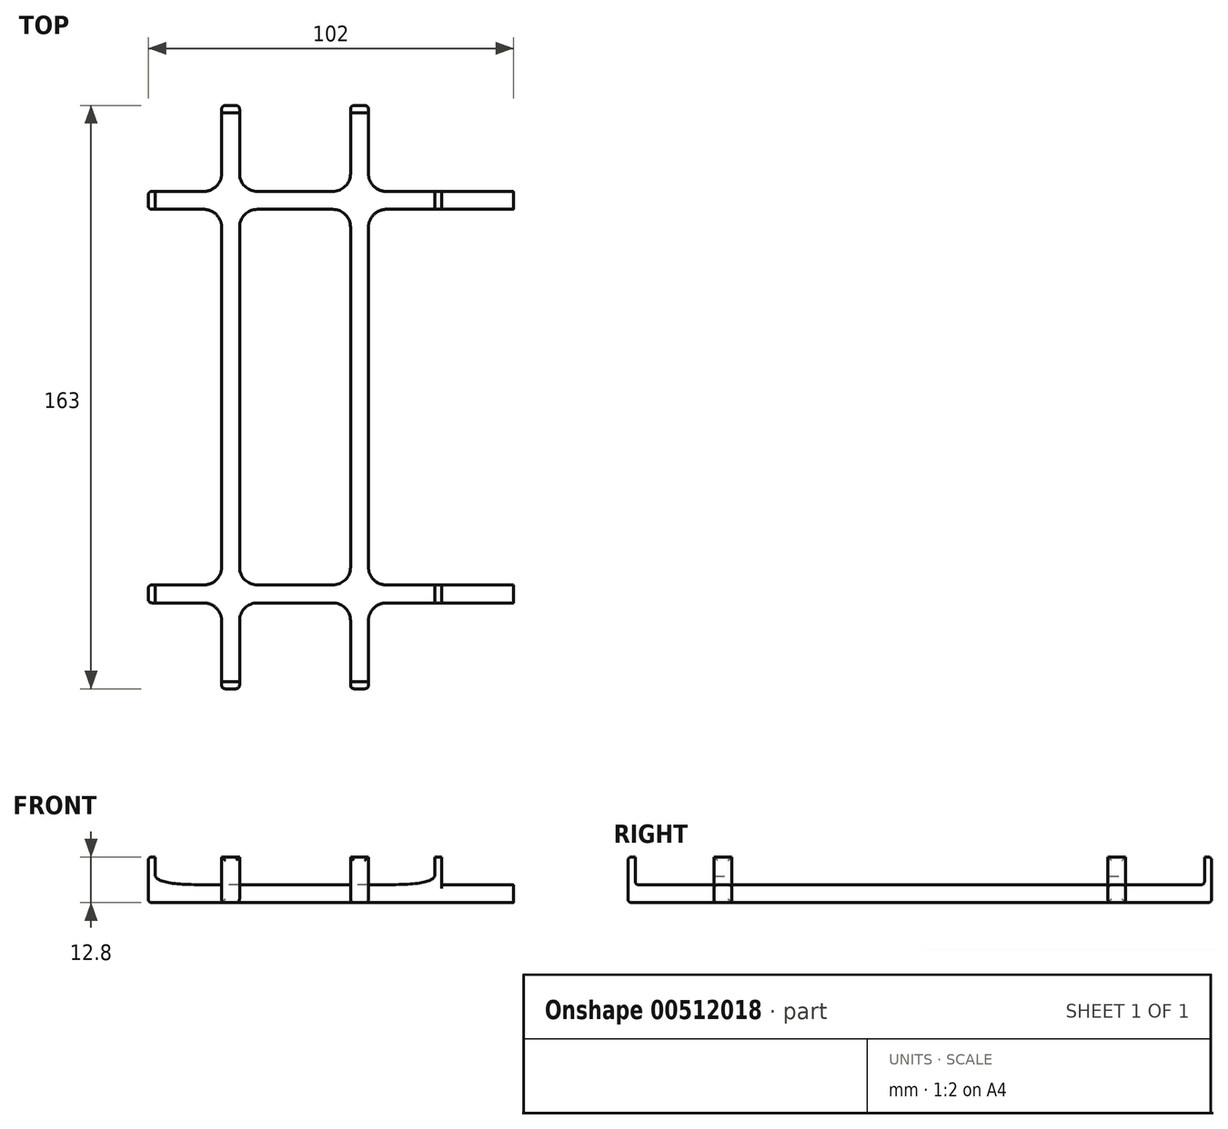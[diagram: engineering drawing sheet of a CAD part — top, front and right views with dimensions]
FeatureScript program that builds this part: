
annotation { "Feature Type Name" : "Feature", "Feature Type Description" : "" }
export const myFeature = defineFeature(function(context is Context, id is Id, definition is map)
    precondition{}
    {
        {
            var Q0;
            Q0=qCreatedBy(makeId("Front.planeOp"),FACE);
            var sketch = newSketch(context, id + "F0", { "sketchPlane" : qUnion([Q0])});
            skLineSegment(sketch, "E0", {"start": v(-41, 7.8) * mm, "end": v(-41, -5) * mm});
            skLineSegment(sketch, "E1", {"start": v(-41, -5) * mm, "end": v(41, -5) * mm});
            skLineSegment(sketch, "E2", {"start": v(41, -5) * mm, "end": v(41, 7.8) * mm});
            skLineSegment(sketch, "E3", {"start": v(41, 7.8) * mm, "end": v(39, 7.8) * mm});
            skLineSegment(sketch, "E4", {"start": v(39, 7.8) * mm, "end": v(39, 0) * mm});
            skLineSegment(sketch, "E5", {"start": v(39, 0) * mm, "end": v(-39, 0) * mm});
            skLineSegment(sketch, "E6", {"start": v(-39, 0) * mm, "end": v(-39, 7.8) * mm});
            skLineSegment(sketch, "E7", {"start": v(-39, 7.8) * mm, "end": v(-41, 7.8) * mm});
            skPoint(sketch, "E8", {"position": v(0, 0) * mm});
            skFitSpline(sketch, "E9", {"points": [v(-39, 2.4) * mm, v(-21, 0) * mm], "startDerivative": vector(3.6, -7.2) * mm, "endDerivative": vector(27, 0) * mm});
            skFitSpline(sketch, "E10.MirrorCS", {"points": [v(39, 2.4) * mm, v(21, 0) * mm], "startDerivative": vector(-3.6, -7.2) * mm, "endDerivative": vector(-27, 0) * mm});
            skSolve(sketch);
        }
        {
            var Q0;
            Q0=makeQuery(id+"F0.imprint","IMPRINT",FACE,{"disambiguationData":[TD([[makeQuery(id+"F0.imprint","IMPRINT",EDGE,{"derivedFrom":sQuery(id+"F0.wireOp",EDGE,"E0")}),1.0]])]});
            var Q1;
            {var subQ3=sQuery(id+"F0.wireOp",EDGE,"E9");Q1=makeQuery(id+"F0.imprint","IMPRINT",FACE,{"disambiguationData":[TD([[makeQuery(id+"F0.imprint","IMPRINT",EDGE,{"derivedFrom":subQ3}),-1.0]])]});}
            var Q2;
            {var subQ3=sQuery(id+"F0.wireOp",EDGE,"E10.MirrorCS");Q2=makeQuery(id+"F0.imprint","IMPRINT",FACE,{"disambiguationData":[TD([[makeQuery(id+"F0.imprint","IMPRINT",EDGE,{"derivedFrom":subQ3}),1.0]])]});}
            extrude(context, id + "F1", {"entities" : qUnion([Q0, Q1, Q2]), "depth" : 5 * mm, "symmetric" : true});
        }
        {
            var Q0;
            Q0=qCreatedBy(makeId("Right.planeOp"),FACE);
            var sketch = newSketch(context, id + "F2", { "sketchPlane" : qUnion([Q0])});
            skLineSegment(sketch, "E11", {"start": v(-81.5, 7.8) * mm, "end": v(-81.5, -5) * mm});
            skLineSegment(sketch, "E12", {"start": v(-81.5, -5) * mm, "end": v(81.5, -5) * mm});
            skLineSegment(sketch, "E13", {"start": v(81.5, -5) * mm, "end": v(81.5, 7.8) * mm});
            skLineSegment(sketch, "E14", {"start": v(81.5, 7.8) * mm, "end": v(79.5, 7.8) * mm});
            skLineSegment(sketch, "E15", {"start": v(79.5, 7.8) * mm, "end": v(79.5, 0) * mm});
            skLineSegment(sketch, "E16", {"start": v(79.5, 0) * mm, "end": v(-79.5, 0) * mm});
            skLineSegment(sketch, "E17", {"start": v(-79.5, 0) * mm, "end": v(-79.5, 7.8) * mm});
            skLineSegment(sketch, "E18", {"start": v(-79.5, 7.8) * mm, "end": v(-81.5, 7.8) * mm});
            skPoint(sketch, "E19", {"position": v(0, 0) * mm});
            skSolve(sketch);
        }
        {
            var Q0;
            Q0=makeQuery(id+"F2.imprint","IMPRINT",FACE,{"disambiguationData":[TD([[makeQuery(id+"F2.imprint","IMPRINT",EDGE,{"derivedFrom":sQuery(id+"F2.wireOp",EDGE,"E11")}),1.0]])]});
            extrude(context, id + "F3", {"entities" : qUnion([Q0]), "depth" : 5 * mm, "symmetric" : true});
        }
        {
            var Q0;
            Q0=makeQuery(id+"F1.opExtrude","SWEPT_BODY",BODY,{"disambiguationData":[OSD([sQuery(id+"F0.wireOp",EDGE,"E0"),sQuery(id+"F0.wireOp",EDGE,"E1"),sQuery(id+"F0.wireOp",EDGE,"E2"),sQuery(id+"F0.wireOp",EDGE,"E3"),sQuery(id+"F0.wireOp",EDGE,"E4"),sQuery(id+"F0.wireOp",EDGE,"E5"),sQuery(id+"F0.wireOp",EDGE,"E6"),sQuery(id+"F0.wireOp",EDGE,"E7"),sQuery(id+"F0.wireOp",EDGE,"E9"),sQuery(id+"F0.wireOp",EDGE,"E10.MirrorCS")])]});
            var Q1;
            Q1=makeQuery(id+"F3.opExtrude","CAP_EDGE",EDGE,{"disambiguationData":[OSD([sQuery(id+"F2.wireOp",EDGE,"E16")])],"isStart":false});
            transform(context, id + "F4", {"entities" : qUnion([Q0]), "transformType" : TransformType.TRANSLATION_DISTANCE, "transformDirection" : qUnion([Q1]), "distance" : 55 * mm, "makeCopy" : false});
        }
        {
            var Q0;
            Q0=makeQuery(id+"F1.opExtrude","SWEPT_BODY",BODY,{"disambiguationData":[OSD([sQuery(id+"F0.wireOp",EDGE,"E0"),sQuery(id+"F0.wireOp",EDGE,"E1"),sQuery(id+"F0.wireOp",EDGE,"E2"),sQuery(id+"F0.wireOp",EDGE,"E3"),sQuery(id+"F0.wireOp",EDGE,"E4"),sQuery(id+"F0.wireOp",EDGE,"E5"),sQuery(id+"F0.wireOp",EDGE,"E6"),sQuery(id+"F0.wireOp",EDGE,"E7"),sQuery(id+"F0.wireOp",EDGE,"E9"),sQuery(id+"F0.wireOp",EDGE,"E10.MirrorCS")])]});
            var Q1;
            Q1=makeQuery(id+"F3.opExtrude","CAP_EDGE",EDGE,{"disambiguationData":[OSD([sQuery(id+"F2.wireOp",EDGE,"E16")])],"isStart":false});
            transform(context, id + "F5", {"entities" : qUnion([Q0]), "transformType" : TransformType.TRANSLATION_DISTANCE, "transformDirection" : qUnion([Q1]), "distance" : 110 * mm, "oppositeDirection" : true, "makeCopy" : true});
        }
        {
            var Q0;
            Q0=makeQuery(id+"F3.opExtrude","SWEPT_BODY",BODY,{"disambiguationData":[OSD([sQuery(id+"F2.wireOp",EDGE,"E11"),sQuery(id+"F2.wireOp",EDGE,"E12"),sQuery(id+"F2.wireOp",EDGE,"E13"),sQuery(id+"F2.wireOp",EDGE,"E14"),sQuery(id+"F2.wireOp",EDGE,"E15"),sQuery(id+"F2.wireOp",EDGE,"E16"),sQuery(id+"F2.wireOp",EDGE,"E17"),sQuery(id+"F2.wireOp",EDGE,"E18")])]});
            var Q1;
            Q1=makeQuery(id+"F1.opExtrude","CAP_EDGE",EDGE,{"disambiguationData":[OSD([sQuery(id+"F0.wireOp",EDGE,"E5")])],"isStart":false});
            transform(context, id + "F6", {"entities" : qUnion([Q0]), "transformType" : TransformType.TRANSLATION_DISTANCE, "transformDirection" : qUnion([Q1]), "distance" : 18 * mm, "makeCopy" : false});
        }
        {
            var Q0;
            Q0=makeQuery(id+"F3.opExtrude","SWEPT_BODY",BODY,{"disambiguationData":[OSD([sQuery(id+"F2.wireOp",EDGE,"E11"),sQuery(id+"F2.wireOp",EDGE,"E12"),sQuery(id+"F2.wireOp",EDGE,"E13"),sQuery(id+"F2.wireOp",EDGE,"E14"),sQuery(id+"F2.wireOp",EDGE,"E15"),sQuery(id+"F2.wireOp",EDGE,"E16"),sQuery(id+"F2.wireOp",EDGE,"E17"),sQuery(id+"F2.wireOp",EDGE,"E18")])]});
            var Q1;
            Q1=makeQuery(id+"F1.opExtrude","CAP_EDGE",EDGE,{"disambiguationData":[OSD([sQuery(id+"F0.wireOp",EDGE,"E5")])],"isStart":true});
            transform(context, id + "F7", {"entities" : qUnion([Q0]), "transformType" : TransformType.TRANSLATION_DISTANCE, "transformDirection" : qUnion([Q1]), "distance" : 36 * mm, "oppositeDirection" : true, "makeCopy" : true});
        }
        {
            var Q0;
            Q0=makeQuery(id+"F1.opExtrude","SWEPT_BODY",BODY,{"disambiguationData":[OSD([sQuery(id+"F0.wireOp",EDGE,"E0"),sQuery(id+"F0.wireOp",EDGE,"E1"),sQuery(id+"F0.wireOp",EDGE,"E2"),sQuery(id+"F0.wireOp",EDGE,"E3"),sQuery(id+"F0.wireOp",EDGE,"E4"),sQuery(id+"F0.wireOp",EDGE,"E5"),sQuery(id+"F0.wireOp",EDGE,"E6"),sQuery(id+"F0.wireOp",EDGE,"E7"),sQuery(id+"F0.wireOp",EDGE,"E9"),sQuery(id+"F0.wireOp",EDGE,"E10.MirrorCS")])]});
            var Q1;
            Q1=makeQuery(id+"F3.opExtrude","SWEPT_BODY",BODY,{"disambiguationData":[OSD([sQuery(id+"F2.wireOp",EDGE,"E11"),sQuery(id+"F2.wireOp",EDGE,"E12"),sQuery(id+"F2.wireOp",EDGE,"E13"),sQuery(id+"F2.wireOp",EDGE,"E14"),sQuery(id+"F2.wireOp",EDGE,"E15"),sQuery(id+"F2.wireOp",EDGE,"E16"),sQuery(id+"F2.wireOp",EDGE,"E17"),sQuery(id+"F2.wireOp",EDGE,"E18")])]});
            var Q2;
            Q2=makeQuery(id+"F7.opPattern","COPY",BODY,{"derivedFrom":makeQuery(id+"F3.opExtrude","SWEPT_BODY",BODY,{"disambiguationData":[OSD([sQuery(id+"F2.wireOp",EDGE,"E11"),sQuery(id+"F2.wireOp",EDGE,"E12"),sQuery(id+"F2.wireOp",EDGE,"E13"),sQuery(id+"F2.wireOp",EDGE,"E14"),sQuery(id+"F2.wireOp",EDGE,"E15"),sQuery(id+"F2.wireOp",EDGE,"E16"),sQuery(id+"F2.wireOp",EDGE,"E17"),sQuery(id+"F2.wireOp",EDGE,"E18")])]}),"instanceName":"1"});
            var Q3;
            Q3=makeQuery(id+"F5.opPattern","COPY",BODY,{"derivedFrom":makeQuery(id+"F1.opExtrude","SWEPT_BODY",BODY,{"disambiguationData":[OSD([sQuery(id+"F0.wireOp",EDGE,"E0"),sQuery(id+"F0.wireOp",EDGE,"E1"),sQuery(id+"F0.wireOp",EDGE,"E2"),sQuery(id+"F0.wireOp",EDGE,"E3"),sQuery(id+"F0.wireOp",EDGE,"E4"),sQuery(id+"F0.wireOp",EDGE,"E5"),sQuery(id+"F0.wireOp",EDGE,"E6"),sQuery(id+"F0.wireOp",EDGE,"E7"),sQuery(id+"F0.wireOp",EDGE,"E9"),sQuery(id+"F0.wireOp",EDGE,"E10.MirrorCS")])]}),"instanceName":"1"});
            booleanBodies(context, id + "F8", {"operationType" : BooleanOperationType.UNION, "tools" : qUnion([Q0, Q1, Q2, Q3])});
        }
        {
            var Q0;
            Q0=makeQuery(id+"F1.opExtrude","SWEPT_FACE",FACE,{"disambiguationData":[OSD([sQuery(id+"F0.wireOp",EDGE,"E2")])]});
            var sketch = newSketch(context, id + "F9", { "sketchPlane" : qUnion([Q0])});
            skLineSegment(sketch, "E20.bottom", {"start": v(-52.5, -5) * mm, "end": v(-57.5, -5) * mm});
            skLineSegment(sketch, "E20.top", {"start": v(-52.5, 0) * mm, "end": v(-57.5, 0) * mm});
            skLineSegment(sketch, "E20.left", {"start": v(-52.5, -5) * mm, "end": v(-52.5, 0) * mm});
            skLineSegment(sketch, "E20.right", {"start": v(-57.5, -5) * mm, "end": v(-57.5, 0) * mm});
            skSolve(sketch);
        }
        {
            var Q0;
            Q0=makeQuery(id+"F9.imprint","IMPRINT",FACE,{"disambiguationData":[TD([[makeQuery(id+"F9.imprint","IMPRINT",EDGE,{"derivedFrom":sQuery(id+"F9.wireOp",EDGE,"E20.bottom")}),1.0]])]});
            extrude(context, id + "F10", {"entities" : qUnion([Q0]), "operationType" : NewBodyOperationType.ADD, "depth" : 20 * mm});
        }
        {
            var Q0;
            Q0=makeQuery(id+"F5.opPattern","COPY",FACE,{"derivedFrom":makeQuery(id+"F1.opExtrude","SWEPT_FACE",FACE,{"disambiguationData":[OSD([sQuery(id+"F0.wireOp",EDGE,"E2")])]}),"instanceName":"1"});
            var sketch = newSketch(context, id + "F11", { "sketchPlane" : qUnion([Q0])});
            skLineSegment(sketch, "E21.bottom", {"start": v(57.5, -5) * mm, "end": v(52.5, -5) * mm});
            skLineSegment(sketch, "E21.top", {"start": v(57.5, 0) * mm, "end": v(52.5, 0) * mm});
            skLineSegment(sketch, "E21.left", {"start": v(57.5, -5) * mm, "end": v(57.5, 0) * mm});
            skLineSegment(sketch, "E21.right", {"start": v(52.5, -5) * mm, "end": v(52.5, 0) * mm});
            skSolve(sketch);
        }
        {
            var Q0;
            Q0=makeQuery(id+"F11.imprint","IMPRINT",FACE,{"disambiguationData":[TD([[makeQuery(id+"F11.imprint","IMPRINT",EDGE,{"derivedFrom":sQuery(id+"F11.wireOp",EDGE,"E21.bottom")}),1.0]])]});
            extrude(context, id + "F12", {"entities" : qUnion([Q0]), "operationType" : NewBodyOperationType.ADD, "depth" : 20 * mm});
        }
        {
            var Q0;
            Q0=makeQuery(id+"F8.opBoolean","INTERSECT",EDGE,{"derivedFrom":[makeQuery(id+"F3.opExtrude","CAP_FACE",FACE,{"disambiguationData":[OSD([sQuery(id+"F2.wireOp",EDGE,"E11"),sQuery(id+"F2.wireOp",EDGE,"E12"),sQuery(id+"F2.wireOp",EDGE,"E13"),sQuery(id+"F2.wireOp",EDGE,"E14"),sQuery(id+"F2.wireOp",EDGE,"E15"),sQuery(id+"F2.wireOp",EDGE,"E16"),sQuery(id+"F2.wireOp",EDGE,"E17"),sQuery(id+"F2.wireOp",EDGE,"E18")])],"isStart":false}),makeQuery(id+"F5.opPattern","COPY",FACE,{"derivedFrom":makeQuery(id+"F1.opExtrude","CAP_FACE",FACE,{"disambiguationData":[OSD([sQuery(id+"F0.wireOp",EDGE,"E0"),sQuery(id+"F0.wireOp",EDGE,"E1"),sQuery(id+"F0.wireOp",EDGE,"E2"),sQuery(id+"F0.wireOp",EDGE,"E3"),sQuery(id+"F0.wireOp",EDGE,"E4"),sQuery(id+"F0.wireOp",EDGE,"E5"),sQuery(id+"F0.wireOp",EDGE,"E6"),sQuery(id+"F0.wireOp",EDGE,"E7"),sQuery(id+"F0.wireOp",EDGE,"E9"),sQuery(id+"F0.wireOp",EDGE,"E10.MirrorCS")])],"isStart":false}),"instanceName":"1"})]});
            var Q1;
            Q1=makeQuery(id+"F8.opBoolean","INTERSECT",EDGE,{"derivedFrom":[makeQuery(id+"F3.opExtrude","CAP_FACE",FACE,{"disambiguationData":[OSD([sQuery(id+"F2.wireOp",EDGE,"E11"),sQuery(id+"F2.wireOp",EDGE,"E12"),sQuery(id+"F2.wireOp",EDGE,"E13"),sQuery(id+"F2.wireOp",EDGE,"E14"),sQuery(id+"F2.wireOp",EDGE,"E15"),sQuery(id+"F2.wireOp",EDGE,"E16"),sQuery(id+"F2.wireOp",EDGE,"E17"),sQuery(id+"F2.wireOp",EDGE,"E18")])],"isStart":false}),makeQuery(id+"F5.opPattern","COPY",FACE,{"derivedFrom":makeQuery(id+"F1.opExtrude","CAP_FACE",FACE,{"disambiguationData":[OSD([sQuery(id+"F0.wireOp",EDGE,"E0"),sQuery(id+"F0.wireOp",EDGE,"E1"),sQuery(id+"F0.wireOp",EDGE,"E2"),sQuery(id+"F0.wireOp",EDGE,"E3"),sQuery(id+"F0.wireOp",EDGE,"E4"),sQuery(id+"F0.wireOp",EDGE,"E5"),sQuery(id+"F0.wireOp",EDGE,"E6"),sQuery(id+"F0.wireOp",EDGE,"E7"),sQuery(id+"F0.wireOp",EDGE,"E9"),sQuery(id+"F0.wireOp",EDGE,"E10.MirrorCS")])],"isStart":true}),"instanceName":"1"})]});
            var Q2;
            Q2=makeQuery(id+"F8.opBoolean","INTERSECT",EDGE,{"derivedFrom":[makeQuery(id+"F3.opExtrude","CAP_FACE",FACE,{"disambiguationData":[OSD([sQuery(id+"F2.wireOp",EDGE,"E11"),sQuery(id+"F2.wireOp",EDGE,"E12"),sQuery(id+"F2.wireOp",EDGE,"E13"),sQuery(id+"F2.wireOp",EDGE,"E14"),sQuery(id+"F2.wireOp",EDGE,"E15"),sQuery(id+"F2.wireOp",EDGE,"E16"),sQuery(id+"F2.wireOp",EDGE,"E17"),sQuery(id+"F2.wireOp",EDGE,"E18")])],"isStart":true}),makeQuery(id+"F5.opPattern","COPY",FACE,{"derivedFrom":makeQuery(id+"F1.opExtrude","CAP_FACE",FACE,{"disambiguationData":[OSD([sQuery(id+"F0.wireOp",EDGE,"E0"),sQuery(id+"F0.wireOp",EDGE,"E1"),sQuery(id+"F0.wireOp",EDGE,"E2"),sQuery(id+"F0.wireOp",EDGE,"E3"),sQuery(id+"F0.wireOp",EDGE,"E4"),sQuery(id+"F0.wireOp",EDGE,"E5"),sQuery(id+"F0.wireOp",EDGE,"E6"),sQuery(id+"F0.wireOp",EDGE,"E7"),sQuery(id+"F0.wireOp",EDGE,"E9"),sQuery(id+"F0.wireOp",EDGE,"E10.MirrorCS")])],"isStart":false}),"instanceName":"1"})]});
            var Q3;
            Q3=makeQuery(id+"F8.opBoolean","INTERSECT",EDGE,{"derivedFrom":[makeQuery(id+"F3.opExtrude","CAP_FACE",FACE,{"disambiguationData":[OSD([sQuery(id+"F2.wireOp",EDGE,"E11"),sQuery(id+"F2.wireOp",EDGE,"E12"),sQuery(id+"F2.wireOp",EDGE,"E13"),sQuery(id+"F2.wireOp",EDGE,"E14"),sQuery(id+"F2.wireOp",EDGE,"E15"),sQuery(id+"F2.wireOp",EDGE,"E16"),sQuery(id+"F2.wireOp",EDGE,"E17"),sQuery(id+"F2.wireOp",EDGE,"E18")])],"isStart":true}),makeQuery(id+"F5.opPattern","COPY",FACE,{"derivedFrom":makeQuery(id+"F1.opExtrude","CAP_FACE",FACE,{"disambiguationData":[OSD([sQuery(id+"F0.wireOp",EDGE,"E0"),sQuery(id+"F0.wireOp",EDGE,"E1"),sQuery(id+"F0.wireOp",EDGE,"E2"),sQuery(id+"F0.wireOp",EDGE,"E3"),sQuery(id+"F0.wireOp",EDGE,"E4"),sQuery(id+"F0.wireOp",EDGE,"E5"),sQuery(id+"F0.wireOp",EDGE,"E6"),sQuery(id+"F0.wireOp",EDGE,"E7"),sQuery(id+"F0.wireOp",EDGE,"E9"),sQuery(id+"F0.wireOp",EDGE,"E10.MirrorCS")])],"isStart":true}),"instanceName":"1"})]});
            var Q4;
            Q4=makeQuery(id+"F8.opBoolean","INTERSECT",EDGE,{"derivedFrom":[makeQuery(id+"F5.opPattern","COPY",FACE,{"derivedFrom":makeQuery(id+"F1.opExtrude","CAP_FACE",FACE,{"disambiguationData":[OSD([sQuery(id+"F0.wireOp",EDGE,"E0"),sQuery(id+"F0.wireOp",EDGE,"E1"),sQuery(id+"F0.wireOp",EDGE,"E2"),sQuery(id+"F0.wireOp",EDGE,"E3"),sQuery(id+"F0.wireOp",EDGE,"E4"),sQuery(id+"F0.wireOp",EDGE,"E5"),sQuery(id+"F0.wireOp",EDGE,"E6"),sQuery(id+"F0.wireOp",EDGE,"E7"),sQuery(id+"F0.wireOp",EDGE,"E9"),sQuery(id+"F0.wireOp",EDGE,"E10.MirrorCS")])],"isStart":true}),"instanceName":"1"}),makeQuery(id+"F7.opPattern","COPY",FACE,{"derivedFrom":makeQuery(id+"F3.opExtrude","CAP_FACE",FACE,{"disambiguationData":[OSD([sQuery(id+"F2.wireOp",EDGE,"E11"),sQuery(id+"F2.wireOp",EDGE,"E12"),sQuery(id+"F2.wireOp",EDGE,"E13"),sQuery(id+"F2.wireOp",EDGE,"E14"),sQuery(id+"F2.wireOp",EDGE,"E15"),sQuery(id+"F2.wireOp",EDGE,"E16"),sQuery(id+"F2.wireOp",EDGE,"E17"),sQuery(id+"F2.wireOp",EDGE,"E18")])],"isStart":true}),"instanceName":"1"})]});
            var Q5;
            Q5=makeQuery(id+"F8.opBoolean","INTERSECT",EDGE,{"derivedFrom":[makeQuery(id+"F5.opPattern","COPY",FACE,{"derivedFrom":makeQuery(id+"F1.opExtrude","CAP_FACE",FACE,{"disambiguationData":[OSD([sQuery(id+"F0.wireOp",EDGE,"E0"),sQuery(id+"F0.wireOp",EDGE,"E1"),sQuery(id+"F0.wireOp",EDGE,"E2"),sQuery(id+"F0.wireOp",EDGE,"E3"),sQuery(id+"F0.wireOp",EDGE,"E4"),sQuery(id+"F0.wireOp",EDGE,"E5"),sQuery(id+"F0.wireOp",EDGE,"E6"),sQuery(id+"F0.wireOp",EDGE,"E7"),sQuery(id+"F0.wireOp",EDGE,"E9"),sQuery(id+"F0.wireOp",EDGE,"E10.MirrorCS")])],"isStart":false}),"instanceName":"1"}),makeQuery(id+"F7.opPattern","COPY",FACE,{"derivedFrom":makeQuery(id+"F3.opExtrude","CAP_FACE",FACE,{"disambiguationData":[OSD([sQuery(id+"F2.wireOp",EDGE,"E11"),sQuery(id+"F2.wireOp",EDGE,"E12"),sQuery(id+"F2.wireOp",EDGE,"E13"),sQuery(id+"F2.wireOp",EDGE,"E14"),sQuery(id+"F2.wireOp",EDGE,"E15"),sQuery(id+"F2.wireOp",EDGE,"E16"),sQuery(id+"F2.wireOp",EDGE,"E17"),sQuery(id+"F2.wireOp",EDGE,"E18")])],"isStart":true}),"instanceName":"1"})]});
            var Q6;
            Q6=makeQuery(id+"F8.opBoolean","INTERSECT",EDGE,{"derivedFrom":[makeQuery(id+"F5.opPattern","COPY",FACE,{"derivedFrom":makeQuery(id+"F1.opExtrude","CAP_FACE",FACE,{"disambiguationData":[OSD([sQuery(id+"F0.wireOp",EDGE,"E0"),sQuery(id+"F0.wireOp",EDGE,"E1"),sQuery(id+"F0.wireOp",EDGE,"E2"),sQuery(id+"F0.wireOp",EDGE,"E3"),sQuery(id+"F0.wireOp",EDGE,"E4"),sQuery(id+"F0.wireOp",EDGE,"E5"),sQuery(id+"F0.wireOp",EDGE,"E6"),sQuery(id+"F0.wireOp",EDGE,"E7"),sQuery(id+"F0.wireOp",EDGE,"E9"),sQuery(id+"F0.wireOp",EDGE,"E10.MirrorCS")])],"isStart":true}),"instanceName":"1"}),makeQuery(id+"F7.opPattern","COPY",FACE,{"derivedFrom":makeQuery(id+"F3.opExtrude","CAP_FACE",FACE,{"disambiguationData":[OSD([sQuery(id+"F2.wireOp",EDGE,"E11"),sQuery(id+"F2.wireOp",EDGE,"E12"),sQuery(id+"F2.wireOp",EDGE,"E13"),sQuery(id+"F2.wireOp",EDGE,"E14"),sQuery(id+"F2.wireOp",EDGE,"E15"),sQuery(id+"F2.wireOp",EDGE,"E16"),sQuery(id+"F2.wireOp",EDGE,"E17"),sQuery(id+"F2.wireOp",EDGE,"E18")])],"isStart":false}),"instanceName":"1"})]});
            var Q7;
            Q7=makeQuery(id+"F8.opBoolean","INTERSECT",EDGE,{"derivedFrom":[makeQuery(id+"F5.opPattern","COPY",FACE,{"derivedFrom":makeQuery(id+"F1.opExtrude","CAP_FACE",FACE,{"disambiguationData":[OSD([sQuery(id+"F0.wireOp",EDGE,"E0"),sQuery(id+"F0.wireOp",EDGE,"E1"),sQuery(id+"F0.wireOp",EDGE,"E2"),sQuery(id+"F0.wireOp",EDGE,"E3"),sQuery(id+"F0.wireOp",EDGE,"E4"),sQuery(id+"F0.wireOp",EDGE,"E5"),sQuery(id+"F0.wireOp",EDGE,"E6"),sQuery(id+"F0.wireOp",EDGE,"E7"),sQuery(id+"F0.wireOp",EDGE,"E9"),sQuery(id+"F0.wireOp",EDGE,"E10.MirrorCS")])],"isStart":false}),"instanceName":"1"}),makeQuery(id+"F7.opPattern","COPY",FACE,{"derivedFrom":makeQuery(id+"F3.opExtrude","CAP_FACE",FACE,{"disambiguationData":[OSD([sQuery(id+"F2.wireOp",EDGE,"E11"),sQuery(id+"F2.wireOp",EDGE,"E12"),sQuery(id+"F2.wireOp",EDGE,"E13"),sQuery(id+"F2.wireOp",EDGE,"E14"),sQuery(id+"F2.wireOp",EDGE,"E15"),sQuery(id+"F2.wireOp",EDGE,"E16"),sQuery(id+"F2.wireOp",EDGE,"E17"),sQuery(id+"F2.wireOp",EDGE,"E18")])],"isStart":false}),"instanceName":"1"})]});
            var Q8;
            Q8=makeQuery(id+"F8.opBoolean","INTERSECT",EDGE,{"derivedFrom":[makeQuery(id+"F1.opExtrude","CAP_FACE",FACE,{"disambiguationData":[OSD([sQuery(id+"F0.wireOp",EDGE,"E0"),sQuery(id+"F0.wireOp",EDGE,"E1"),sQuery(id+"F0.wireOp",EDGE,"E2"),sQuery(id+"F0.wireOp",EDGE,"E3"),sQuery(id+"F0.wireOp",EDGE,"E4"),sQuery(id+"F0.wireOp",EDGE,"E5"),sQuery(id+"F0.wireOp",EDGE,"E6"),sQuery(id+"F0.wireOp",EDGE,"E7"),sQuery(id+"F0.wireOp",EDGE,"E9"),sQuery(id+"F0.wireOp",EDGE,"E10.MirrorCS")])],"isStart":false}),makeQuery(id+"F7.opPattern","COPY",FACE,{"derivedFrom":makeQuery(id+"F3.opExtrude","CAP_FACE",FACE,{"disambiguationData":[OSD([sQuery(id+"F2.wireOp",EDGE,"E11"),sQuery(id+"F2.wireOp",EDGE,"E12"),sQuery(id+"F2.wireOp",EDGE,"E13"),sQuery(id+"F2.wireOp",EDGE,"E14"),sQuery(id+"F2.wireOp",EDGE,"E15"),sQuery(id+"F2.wireOp",EDGE,"E16"),sQuery(id+"F2.wireOp",EDGE,"E17"),sQuery(id+"F2.wireOp",EDGE,"E18")])],"isStart":false}),"instanceName":"1"})]});
            var Q9;
            Q9=makeQuery(id+"F8.opBoolean","INTERSECT",EDGE,{"derivedFrom":[makeQuery(id+"F1.opExtrude","CAP_FACE",FACE,{"disambiguationData":[OSD([sQuery(id+"F0.wireOp",EDGE,"E0"),sQuery(id+"F0.wireOp",EDGE,"E1"),sQuery(id+"F0.wireOp",EDGE,"E2"),sQuery(id+"F0.wireOp",EDGE,"E3"),sQuery(id+"F0.wireOp",EDGE,"E4"),sQuery(id+"F0.wireOp",EDGE,"E5"),sQuery(id+"F0.wireOp",EDGE,"E6"),sQuery(id+"F0.wireOp",EDGE,"E7"),sQuery(id+"F0.wireOp",EDGE,"E9"),sQuery(id+"F0.wireOp",EDGE,"E10.MirrorCS")])],"isStart":true}),makeQuery(id+"F7.opPattern","COPY",FACE,{"derivedFrom":makeQuery(id+"F3.opExtrude","CAP_FACE",FACE,{"disambiguationData":[OSD([sQuery(id+"F2.wireOp",EDGE,"E11"),sQuery(id+"F2.wireOp",EDGE,"E12"),sQuery(id+"F2.wireOp",EDGE,"E13"),sQuery(id+"F2.wireOp",EDGE,"E14"),sQuery(id+"F2.wireOp",EDGE,"E15"),sQuery(id+"F2.wireOp",EDGE,"E16"),sQuery(id+"F2.wireOp",EDGE,"E17"),sQuery(id+"F2.wireOp",EDGE,"E18")])],"isStart":false}),"instanceName":"1"})]});
            var Q10;
            Q10=makeQuery(id+"F8.opBoolean","INTERSECT",EDGE,{"derivedFrom":[makeQuery(id+"F1.opExtrude","CAP_FACE",FACE,{"disambiguationData":[OSD([sQuery(id+"F0.wireOp",EDGE,"E0"),sQuery(id+"F0.wireOp",EDGE,"E1"),sQuery(id+"F0.wireOp",EDGE,"E2"),sQuery(id+"F0.wireOp",EDGE,"E3"),sQuery(id+"F0.wireOp",EDGE,"E4"),sQuery(id+"F0.wireOp",EDGE,"E5"),sQuery(id+"F0.wireOp",EDGE,"E6"),sQuery(id+"F0.wireOp",EDGE,"E7"),sQuery(id+"F0.wireOp",EDGE,"E9"),sQuery(id+"F0.wireOp",EDGE,"E10.MirrorCS")])],"isStart":true}),makeQuery(id+"F7.opPattern","COPY",FACE,{"derivedFrom":makeQuery(id+"F3.opExtrude","CAP_FACE",FACE,{"disambiguationData":[OSD([sQuery(id+"F2.wireOp",EDGE,"E11"),sQuery(id+"F2.wireOp",EDGE,"E12"),sQuery(id+"F2.wireOp",EDGE,"E13"),sQuery(id+"F2.wireOp",EDGE,"E14"),sQuery(id+"F2.wireOp",EDGE,"E15"),sQuery(id+"F2.wireOp",EDGE,"E16"),sQuery(id+"F2.wireOp",EDGE,"E17"),sQuery(id+"F2.wireOp",EDGE,"E18")])],"isStart":true}),"instanceName":"1"})]});
            var Q11;
            Q11=makeQuery(id+"F8.opBoolean","INTERSECT",EDGE,{"derivedFrom":[makeQuery(id+"F1.opExtrude","CAP_FACE",FACE,{"disambiguationData":[OSD([sQuery(id+"F0.wireOp",EDGE,"E0"),sQuery(id+"F0.wireOp",EDGE,"E1"),sQuery(id+"F0.wireOp",EDGE,"E2"),sQuery(id+"F0.wireOp",EDGE,"E3"),sQuery(id+"F0.wireOp",EDGE,"E4"),sQuery(id+"F0.wireOp",EDGE,"E5"),sQuery(id+"F0.wireOp",EDGE,"E6"),sQuery(id+"F0.wireOp",EDGE,"E7"),sQuery(id+"F0.wireOp",EDGE,"E9"),sQuery(id+"F0.wireOp",EDGE,"E10.MirrorCS")])],"isStart":false}),makeQuery(id+"F7.opPattern","COPY",FACE,{"derivedFrom":makeQuery(id+"F3.opExtrude","CAP_FACE",FACE,{"disambiguationData":[OSD([sQuery(id+"F2.wireOp",EDGE,"E11"),sQuery(id+"F2.wireOp",EDGE,"E12"),sQuery(id+"F2.wireOp",EDGE,"E13"),sQuery(id+"F2.wireOp",EDGE,"E14"),sQuery(id+"F2.wireOp",EDGE,"E15"),sQuery(id+"F2.wireOp",EDGE,"E16"),sQuery(id+"F2.wireOp",EDGE,"E17"),sQuery(id+"F2.wireOp",EDGE,"E18")])],"isStart":true}),"instanceName":"1"})]});
            var Q12;
            Q12=makeQuery(id+"F8.opBoolean","INTERSECT",EDGE,{"derivedFrom":[makeQuery(id+"F1.opExtrude","CAP_FACE",FACE,{"disambiguationData":[OSD([sQuery(id+"F0.wireOp",EDGE,"E0"),sQuery(id+"F0.wireOp",EDGE,"E1"),sQuery(id+"F0.wireOp",EDGE,"E2"),sQuery(id+"F0.wireOp",EDGE,"E3"),sQuery(id+"F0.wireOp",EDGE,"E4"),sQuery(id+"F0.wireOp",EDGE,"E5"),sQuery(id+"F0.wireOp",EDGE,"E6"),sQuery(id+"F0.wireOp",EDGE,"E7"),sQuery(id+"F0.wireOp",EDGE,"E9"),sQuery(id+"F0.wireOp",EDGE,"E10.MirrorCS")])],"isStart":false}),makeQuery(id+"F3.opExtrude","CAP_FACE",FACE,{"disambiguationData":[OSD([sQuery(id+"F2.wireOp",EDGE,"E11"),sQuery(id+"F2.wireOp",EDGE,"E12"),sQuery(id+"F2.wireOp",EDGE,"E13"),sQuery(id+"F2.wireOp",EDGE,"E14"),sQuery(id+"F2.wireOp",EDGE,"E15"),sQuery(id+"F2.wireOp",EDGE,"E16"),sQuery(id+"F2.wireOp",EDGE,"E17"),sQuery(id+"F2.wireOp",EDGE,"E18")])],"isStart":true})]});
            var Q13;
            Q13=makeQuery(id+"F8.opBoolean","INTERSECT",EDGE,{"derivedFrom":[makeQuery(id+"F1.opExtrude","CAP_FACE",FACE,{"disambiguationData":[OSD([sQuery(id+"F0.wireOp",EDGE,"E0"),sQuery(id+"F0.wireOp",EDGE,"E1"),sQuery(id+"F0.wireOp",EDGE,"E2"),sQuery(id+"F0.wireOp",EDGE,"E3"),sQuery(id+"F0.wireOp",EDGE,"E4"),sQuery(id+"F0.wireOp",EDGE,"E5"),sQuery(id+"F0.wireOp",EDGE,"E6"),sQuery(id+"F0.wireOp",EDGE,"E7"),sQuery(id+"F0.wireOp",EDGE,"E9"),sQuery(id+"F0.wireOp",EDGE,"E10.MirrorCS")])],"isStart":false}),makeQuery(id+"F3.opExtrude","CAP_FACE",FACE,{"disambiguationData":[OSD([sQuery(id+"F2.wireOp",EDGE,"E11"),sQuery(id+"F2.wireOp",EDGE,"E12"),sQuery(id+"F2.wireOp",EDGE,"E13"),sQuery(id+"F2.wireOp",EDGE,"E14"),sQuery(id+"F2.wireOp",EDGE,"E15"),sQuery(id+"F2.wireOp",EDGE,"E16"),sQuery(id+"F2.wireOp",EDGE,"E17"),sQuery(id+"F2.wireOp",EDGE,"E18")])],"isStart":false})]});
            var Q14;
            Q14=makeQuery(id+"F8.opBoolean","INTERSECT",EDGE,{"derivedFrom":[makeQuery(id+"F1.opExtrude","CAP_FACE",FACE,{"disambiguationData":[OSD([sQuery(id+"F0.wireOp",EDGE,"E0"),sQuery(id+"F0.wireOp",EDGE,"E1"),sQuery(id+"F0.wireOp",EDGE,"E2"),sQuery(id+"F0.wireOp",EDGE,"E3"),sQuery(id+"F0.wireOp",EDGE,"E4"),sQuery(id+"F0.wireOp",EDGE,"E5"),sQuery(id+"F0.wireOp",EDGE,"E6"),sQuery(id+"F0.wireOp",EDGE,"E7"),sQuery(id+"F0.wireOp",EDGE,"E9"),sQuery(id+"F0.wireOp",EDGE,"E10.MirrorCS")])],"isStart":true}),makeQuery(id+"F3.opExtrude","CAP_FACE",FACE,{"disambiguationData":[OSD([sQuery(id+"F2.wireOp",EDGE,"E11"),sQuery(id+"F2.wireOp",EDGE,"E12"),sQuery(id+"F2.wireOp",EDGE,"E13"),sQuery(id+"F2.wireOp",EDGE,"E14"),sQuery(id+"F2.wireOp",EDGE,"E15"),sQuery(id+"F2.wireOp",EDGE,"E16"),sQuery(id+"F2.wireOp",EDGE,"E17"),sQuery(id+"F2.wireOp",EDGE,"E18")])],"isStart":false})]});
            var Q15;
            Q15=makeQuery(id+"F8.opBoolean","INTERSECT",EDGE,{"derivedFrom":[makeQuery(id+"F1.opExtrude","CAP_FACE",FACE,{"disambiguationData":[OSD([sQuery(id+"F0.wireOp",EDGE,"E0"),sQuery(id+"F0.wireOp",EDGE,"E1"),sQuery(id+"F0.wireOp",EDGE,"E2"),sQuery(id+"F0.wireOp",EDGE,"E3"),sQuery(id+"F0.wireOp",EDGE,"E4"),sQuery(id+"F0.wireOp",EDGE,"E5"),sQuery(id+"F0.wireOp",EDGE,"E6"),sQuery(id+"F0.wireOp",EDGE,"E7"),sQuery(id+"F0.wireOp",EDGE,"E9"),sQuery(id+"F0.wireOp",EDGE,"E10.MirrorCS")])],"isStart":true}),makeQuery(id+"F3.opExtrude","CAP_FACE",FACE,{"disambiguationData":[OSD([sQuery(id+"F2.wireOp",EDGE,"E11"),sQuery(id+"F2.wireOp",EDGE,"E12"),sQuery(id+"F2.wireOp",EDGE,"E13"),sQuery(id+"F2.wireOp",EDGE,"E14"),sQuery(id+"F2.wireOp",EDGE,"E15"),sQuery(id+"F2.wireOp",EDGE,"E16"),sQuery(id+"F2.wireOp",EDGE,"E17"),sQuery(id+"F2.wireOp",EDGE,"E18")])],"isStart":true})]});
            var Q16;
            Q16=makeQuery(id+"F10.opExtrude","CAP_EDGE",EDGE,{"disambiguationData":[OSD([sQuery(id+"F9.wireOp",EDGE,"E20.top")])],"isStart":true});
            var Q17;
            Q17=makeQuery(id+"F12.opExtrude","CAP_EDGE",EDGE,{"disambiguationData":[OSD([sQuery(id+"F11.wireOp",EDGE,"E21.top")])],"isStart":true});
            fillet(context, id + "F13", {"entities" : qUnion([Q0, Q1, Q2, Q3, Q4, Q5, Q6, Q7, Q8, Q9, Q10, Q11, Q12, Q13, Q14, Q15, Q16, Q17]), "radius" : 5 * mm, "tangentPropagation" : true, "allowEdgeOverflow" : false});
        }
        {
            var Q0;
            Q0=makeQuery(id+"F12.opExtrude","SWEPT_EDGE",EDGE,{"disambiguationData":[OSD([sQuery(id+"F0.wireOp",EDGE,"E2"),sQuery(id+"F11.wireOp",EDGE,"E21.top"),sQuery(id+"F11.wireOp",EDGE,"E21.right")])]});
            var Q1;
            Q1=makeQuery(id+"F12.opExtrude","SWEPT_EDGE",EDGE,{"disambiguationData":[OSD([sQuery(id+"F0.wireOp",EDGE,"E2"),sQuery(id+"F11.wireOp",EDGE,"E21.top"),sQuery(id+"F11.wireOp",EDGE,"E21.left")])]});
            var Q2;
            Q2=makeQuery(id+"F10.opExtrude","SWEPT_EDGE",EDGE,{"disambiguationData":[OSD([sQuery(id+"F0.wireOp",EDGE,"E2"),sQuery(id+"F9.wireOp",EDGE,"E20.top"),sQuery(id+"F9.wireOp",EDGE,"E20.right")])]});
            var Q3;
            Q3=makeQuery(id+"F10.opExtrude","SWEPT_EDGE",EDGE,{"disambiguationData":[OSD([sQuery(id+"F0.wireOp",EDGE,"E2"),sQuery(id+"F9.wireOp",EDGE,"E20.top"),sQuery(id+"F9.wireOp",EDGE,"E20.left")])]});
            var Q4;
            {var subQ2=sQuery(id+"F0.wireOp",EDGE,"E2");var subQ3=sQuery(id+"F0.wireOp",EDGE,"E1");Q4=makeQuery(id+"F10.boolean.opBoolean","MERGE",EDGE,{"derivedFrom":[makeQuery(id+"F8.opBoolean","SPLIT",EDGE,{"disambiguationData":[TD([makeQuery(id+"F1.opExtrude","SWEPT_FACE",FACE,{"disambiguationData":[OSD([subQ2])]})])],"derivedFrom":makeQuery(id+"F1.opExtrude","CAP_EDGE",EDGE,{"disambiguationData":[OSD([subQ3])],"isStart":false})}),makeQuery(id+"F10.opExtrude","SWEPT_EDGE",EDGE,{"disambiguationData":[OSD([sQuery(id+"F9.wireOp",EDGE,"E20.bottom"),sQuery(id+"F9.wireOp",EDGE,"E20.right")])]})]});}
            var Q5;
            {var subQ0=sQuery(id+"F0.wireOp",EDGE,"E2");var subQ3=sQuery(id+"F0.wireOp",EDGE,"E1");Q5=makeQuery(id+"F10.boolean.opBoolean","MERGE",EDGE,{"derivedFrom":[makeQuery(id+"F8.opBoolean","SPLIT",EDGE,{"disambiguationData":[TD([makeQuery(id+"F1.opExtrude","SWEPT_FACE",FACE,{"disambiguationData":[OSD([subQ0])]})])],"derivedFrom":makeQuery(id+"F1.opExtrude","CAP_EDGE",EDGE,{"disambiguationData":[OSD([subQ3])],"isStart":true})}),makeQuery(id+"F10.opExtrude","SWEPT_EDGE",EDGE,{"disambiguationData":[OSD([sQuery(id+"F9.wireOp",EDGE,"E20.bottom"),sQuery(id+"F9.wireOp",EDGE,"E20.left")])]})]});}
            var Q6;
            {var subQ0=sQuery(id+"F0.wireOp",EDGE,"E2");var subQ1=sQuery(id+"F0.wireOp",EDGE,"E1");Q6=makeQuery(id+"F12.boolean.opBoolean","MERGE",EDGE,{"derivedFrom":[makeQuery(id+"F8.opBoolean","SPLIT",EDGE,{"disambiguationData":[TD([makeQuery(id+"F5.opPattern","COPY",FACE,{"derivedFrom":makeQuery(id+"F1.opExtrude","SWEPT_FACE",FACE,{"disambiguationData":[OSD([subQ0])]}),"instanceName":"1"})])],"derivedFrom":makeQuery(id+"F5.opPattern","COPY",EDGE,{"derivedFrom":makeQuery(id+"F1.opExtrude","CAP_EDGE",EDGE,{"disambiguationData":[OSD([subQ1])],"isStart":true}),"instanceName":"1"})}),makeQuery(id+"F12.opExtrude","SWEPT_EDGE",EDGE,{"disambiguationData":[OSD([sQuery(id+"F11.wireOp",EDGE,"E21.bottom"),sQuery(id+"F11.wireOp",EDGE,"E21.left")])]})]});}
            var Q7;
            Q7=makeQuery(id+"F7.opPattern","COPY",EDGE,{"derivedFrom":makeQuery(id+"F3.opExtrude","SWEPT_EDGE",EDGE,{"disambiguationData":[OSD([sQuery(id+"F2.wireOp",EDGE,"E12"),sQuery(id+"F2.wireOp",EDGE,"E13")])]}),"instanceName":"1"});
            var Q8;
            {var subQ1=sQuery(id+"F2.wireOp",EDGE,"E13");var subQ2=sQuery(id+"F2.wireOp",EDGE,"E12");Q8=makeQuery(id+"F8.opBoolean","SPLIT",EDGE,{"disambiguationData":[TD([makeQuery(id+"F7.opPattern","COPY",FACE,{"derivedFrom":makeQuery(id+"F3.opExtrude","SWEPT_FACE",FACE,{"disambiguationData":[OSD([subQ1])]}),"instanceName":"1"})])],"derivedFrom":makeQuery(id+"F7.opPattern","COPY",EDGE,{"derivedFrom":makeQuery(id+"F3.opExtrude","CAP_EDGE",EDGE,{"disambiguationData":[OSD([subQ2])],"isStart":true}),"instanceName":"1"})});}
            var Q9;
            Q9=makeQuery(id+"F3.opExtrude","SWEPT_EDGE",EDGE,{"disambiguationData":[OSD([sQuery(id+"F2.wireOp",EDGE,"E12"),sQuery(id+"F2.wireOp",EDGE,"E13")])]});
            var Q10;
            {var subQ0=sQuery(id+"F2.wireOp",EDGE,"E13");var subQ1=sQuery(id+"F2.wireOp",EDGE,"E12");Q10=makeQuery(id+"F8.opBoolean","SPLIT",EDGE,{"disambiguationData":[TD([makeQuery(id+"F3.opExtrude","SWEPT_FACE",FACE,{"disambiguationData":[OSD([subQ0])]})])],"derivedFrom":makeQuery(id+"F3.opExtrude","CAP_EDGE",EDGE,{"disambiguationData":[OSD([subQ1])],"isStart":true})});}
            var Q11;
            Q11=makeQuery(id+"F5.opPattern","COPY",EDGE,{"derivedFrom":makeQuery(id+"F1.opExtrude","SWEPT_EDGE",EDGE,{"disambiguationData":[OSD([sQuery(id+"F0.wireOp",EDGE,"E0"),sQuery(id+"F0.wireOp",EDGE,"E1")])]}),"instanceName":"1"});
            var Q12;
            {var subQ0=sQuery(id+"F0.wireOp",EDGE,"E0");var subQ3=sQuery(id+"F0.wireOp",EDGE,"E1");Q12=makeQuery(id+"F8.opBoolean","SPLIT",EDGE,{"disambiguationData":[TD([makeQuery(id+"F5.opPattern","COPY",FACE,{"derivedFrom":makeQuery(id+"F1.opExtrude","SWEPT_FACE",FACE,{"disambiguationData":[OSD([subQ0])]}),"instanceName":"1"})])],"derivedFrom":makeQuery(id+"F5.opPattern","COPY",EDGE,{"derivedFrom":makeQuery(id+"F1.opExtrude","CAP_EDGE",EDGE,{"disambiguationData":[OSD([subQ3])],"isStart":false}),"instanceName":"1"})});}
            var Q13;
            Q13=makeQuery(id+"F1.opExtrude","SWEPT_EDGE",EDGE,{"disambiguationData":[OSD([sQuery(id+"F0.wireOp",EDGE,"E0"),sQuery(id+"F0.wireOp",EDGE,"E1")])]});
            var Q14;
            {var subQ1=sQuery(id+"F0.wireOp",EDGE,"E1");var subQ2=sQuery(id+"F0.wireOp",EDGE,"E0");Q14=makeQuery(id+"F8.opBoolean","SPLIT",EDGE,{"disambiguationData":[TD([makeQuery(id+"F1.opExtrude","SWEPT_FACE",FACE,{"disambiguationData":[OSD([subQ2])]})])],"derivedFrom":makeQuery(id+"F1.opExtrude","CAP_EDGE",EDGE,{"disambiguationData":[OSD([subQ1])],"isStart":false})});}
            var Q15;
            Q15=makeQuery(id+"F3.opExtrude","SWEPT_EDGE",EDGE,{"disambiguationData":[OSD([sQuery(id+"F2.wireOp",EDGE,"E11"),sQuery(id+"F2.wireOp",EDGE,"E12")])]});
            var Q16;
            {var subQ0=sQuery(id+"F2.wireOp",EDGE,"E12");var subQ1=sQuery(id+"F2.wireOp",EDGE,"E11");Q16=makeQuery(id+"F8.opBoolean","SPLIT",EDGE,{"disambiguationData":[TD([makeQuery(id+"F3.opExtrude","SWEPT_FACE",FACE,{"disambiguationData":[OSD([subQ1])]})])],"derivedFrom":makeQuery(id+"F3.opExtrude","CAP_EDGE",EDGE,{"disambiguationData":[OSD([subQ0])],"isStart":false})});}
            var Q17;
            Q17=makeQuery(id+"F7.opPattern","COPY",EDGE,{"derivedFrom":makeQuery(id+"F3.opExtrude","SWEPT_EDGE",EDGE,{"disambiguationData":[OSD([sQuery(id+"F2.wireOp",EDGE,"E11"),sQuery(id+"F2.wireOp",EDGE,"E12")])]}),"instanceName":"1"});
            var Q18;
            {var subQ0=sQuery(id+"F2.wireOp",EDGE,"E12");var subQ1=sQuery(id+"F0.wireOp",EDGE,"E1");var subQ4=sQuery(id+"F0.wireOp",EDGE,"E10.MirrorCS");var subQ5=sQuery(id+"F0.wireOp",EDGE,"E9");var subQ6=sQuery(id+"F0.wireOp",EDGE,"E7");var subQ7=sQuery(id+"F0.wireOp",EDGE,"E6");var subQ8=sQuery(id+"F0.wireOp",EDGE,"E5");var subQ9=sQuery(id+"F0.wireOp",EDGE,"E4");var subQ10=sQuery(id+"F0.wireOp",EDGE,"E3");var subQ11=sQuery(id+"F0.wireOp",EDGE,"E2");var subQ12=sQuery(id+"F0.wireOp",EDGE,"E0");Q18=makeQuery(id+"F8.opBoolean","SPLIT",EDGE,{"disambiguationData":[TD([makeQuery(id+"F1.opExtrude","CAP_FACE",FACE,{"disambiguationData":[OSD([subQ12,subQ1,subQ11,subQ10,subQ9,subQ8,subQ7,subQ6,subQ5,subQ4])],"isStart":true})])],"derivedFrom":makeQuery(id+"F3.opExtrude","CAP_EDGE",EDGE,{"disambiguationData":[OSD([subQ0])],"isStart":false})});}
            var Q19;
            Q19=makeQuery(id+"F7.opPattern","COPY",EDGE,{"derivedFrom":makeQuery(id+"F3.opExtrude","SWEPT_EDGE",EDGE,{"disambiguationData":[OSD([sQuery(id+"F2.wireOp",EDGE,"E11"),sQuery(id+"F2.wireOp",EDGE,"E18")])]}),"instanceName":"1"});
            var Q20;
            Q20=makeQuery(id+"F3.opExtrude","SWEPT_EDGE",EDGE,{"disambiguationData":[OSD([sQuery(id+"F2.wireOp",EDGE,"E11"),sQuery(id+"F2.wireOp",EDGE,"E18")])]});
            var Q21;
            Q21=makeQuery(id+"F3.opExtrude","CAP_EDGE",EDGE,{"disambiguationData":[OSD([sQuery(id+"F2.wireOp",EDGE,"E11")])],"isStart":true});
            var Q22;
            Q22=makeQuery(id+"F3.opExtrude","CAP_EDGE",EDGE,{"disambiguationData":[OSD([sQuery(id+"F2.wireOp",EDGE,"E11")])],"isStart":false});
            var Q23;
            Q23=makeQuery(id+"F7.opPattern","COPY",EDGE,{"derivedFrom":makeQuery(id+"F3.opExtrude","CAP_EDGE",EDGE,{"disambiguationData":[OSD([sQuery(id+"F2.wireOp",EDGE,"E11")])],"isStart":true}),"instanceName":"1"});
            var Q24;
            Q24=makeQuery(id+"F7.opPattern","COPY",EDGE,{"derivedFrom":makeQuery(id+"F3.opExtrude","CAP_EDGE",EDGE,{"disambiguationData":[OSD([sQuery(id+"F2.wireOp",EDGE,"E11")])],"isStart":false}),"instanceName":"1"});
            var Q25;
            Q25=makeQuery(id+"F1.opExtrude","CAP_EDGE",EDGE,{"disambiguationData":[OSD([sQuery(id+"F0.wireOp",EDGE,"E0")])],"isStart":false});
            var Q26;
            Q26=makeQuery(id+"F1.opExtrude","CAP_EDGE",EDGE,{"disambiguationData":[OSD([sQuery(id+"F0.wireOp",EDGE,"E0")])],"isStart":true});
            var Q27;
            Q27=makeQuery(id+"F1.opExtrude","SWEPT_EDGE",EDGE,{"disambiguationData":[OSD([sQuery(id+"F0.wireOp",EDGE,"E0"),sQuery(id+"F0.wireOp",EDGE,"E7")])]});
            var Q28;
            Q28=makeQuery(id+"F13.opFillet","BLEND_EDGE",EDGE,{"blendedFrom":[makeQuery(id+"F10.opExtrude","CAP_EDGE",EDGE,{"disambiguationData":[OSD([sQuery(id+"F9.wireOp",EDGE,"E20.top")])],"isStart":true}),makeQuery(id+"F1.opExtrude","SWEPT_FACE",FACE,{"disambiguationData":[OSD([sQuery(id+"F0.wireOp",EDGE,"E3")])]})],"blendedInto":[makeQuery(id+"F1.opExtrude","SWEPT_FACE",FACE,{"disambiguationData":[OSD([sQuery(id+"F0.wireOp",EDGE,"E3")])]})]});
            var Q29;
            Q29=makeQuery(id+"F13.opFillet","BLEND_EDGE",EDGE,{"blendedFrom":[makeQuery(id+"F12.opExtrude","CAP_EDGE",EDGE,{"disambiguationData":[OSD([sQuery(id+"F11.wireOp",EDGE,"E21.top")])],"isStart":true}),makeQuery(id+"F5.opPattern","COPY",FACE,{"derivedFrom":makeQuery(id+"F1.opExtrude","SWEPT_FACE",FACE,{"disambiguationData":[OSD([sQuery(id+"F0.wireOp",EDGE,"E3")])]}),"instanceName":"1"})],"blendedInto":[makeQuery(id+"F5.opPattern","COPY",FACE,{"derivedFrom":makeQuery(id+"F1.opExtrude","SWEPT_FACE",FACE,{"disambiguationData":[OSD([sQuery(id+"F0.wireOp",EDGE,"E3")])]}),"instanceName":"1"})]});
            var Q30;
            Q30=makeQuery(id+"F5.opPattern","COPY",EDGE,{"derivedFrom":makeQuery(id+"F1.opExtrude","CAP_EDGE",EDGE,{"disambiguationData":[OSD([sQuery(id+"F0.wireOp",EDGE,"E0")])],"isStart":false}),"instanceName":"1"});
            var Q31;
            Q31=makeQuery(id+"F5.opPattern","COPY",EDGE,{"derivedFrom":makeQuery(id+"F1.opExtrude","SWEPT_EDGE",EDGE,{"disambiguationData":[OSD([sQuery(id+"F0.wireOp",EDGE,"E0"),sQuery(id+"F0.wireOp",EDGE,"E7")])]}),"instanceName":"1"});
            var Q32;
            Q32=makeQuery(id+"F5.opPattern","COPY",EDGE,{"derivedFrom":makeQuery(id+"F1.opExtrude","CAP_EDGE",EDGE,{"disambiguationData":[OSD([sQuery(id+"F0.wireOp",EDGE,"E0")])],"isStart":true}),"instanceName":"1"});
            var Q33;
            Q33=makeQuery(id+"F3.opExtrude","CAP_EDGE",EDGE,{"disambiguationData":[OSD([sQuery(id+"F2.wireOp",EDGE,"E13")])],"isStart":true});
            var Q34;
            Q34=makeQuery(id+"F3.opExtrude","SWEPT_EDGE",EDGE,{"disambiguationData":[OSD([sQuery(id+"F2.wireOp",EDGE,"E13"),sQuery(id+"F2.wireOp",EDGE,"E14")])]});
            var Q35;
            Q35=makeQuery(id+"F3.opExtrude","CAP_EDGE",EDGE,{"disambiguationData":[OSD([sQuery(id+"F2.wireOp",EDGE,"E13")])],"isStart":false});
            var Q36;
            Q36=makeQuery(id+"F7.opPattern","COPY",EDGE,{"derivedFrom":makeQuery(id+"F3.opExtrude","CAP_EDGE",EDGE,{"disambiguationData":[OSD([sQuery(id+"F2.wireOp",EDGE,"E13")])],"isStart":true}),"instanceName":"1"});
            var Q37;
            Q37=makeQuery(id+"F7.opPattern","COPY",EDGE,{"derivedFrom":makeQuery(id+"F3.opExtrude","SWEPT_EDGE",EDGE,{"disambiguationData":[OSD([sQuery(id+"F2.wireOp",EDGE,"E13"),sQuery(id+"F2.wireOp",EDGE,"E14")])]}),"instanceName":"1"});
            var Q38;
            Q38=makeQuery(id+"F7.opPattern","COPY",EDGE,{"derivedFrom":makeQuery(id+"F3.opExtrude","CAP_EDGE",EDGE,{"disambiguationData":[OSD([sQuery(id+"F2.wireOp",EDGE,"E13")])],"isStart":false}),"instanceName":"1"});
            var Q39;
            Q39=makeQuery(id+"F7.opPattern","COPY",EDGE,{"derivedFrom":makeQuery(id+"F3.opExtrude","SWEPT_EDGE",EDGE,{"disambiguationData":[OSD([sQuery(id+"F2.wireOp",EDGE,"E15"),sQuery(id+"F2.wireOp",EDGE,"E16")])]}),"instanceName":"1"});
            var Q40;
            Q40=makeQuery(id+"F3.opExtrude","SWEPT_EDGE",EDGE,{"disambiguationData":[OSD([sQuery(id+"F2.wireOp",EDGE,"E15"),sQuery(id+"F2.wireOp",EDGE,"E16")])]});
            var Q41;
            Q41=makeQuery(id+"F7.opPattern","COPY",EDGE,{"derivedFrom":makeQuery(id+"F3.opExtrude","SWEPT_EDGE",EDGE,{"disambiguationData":[OSD([sQuery(id+"F2.wireOp",EDGE,"E16"),sQuery(id+"F2.wireOp",EDGE,"E17")])]}),"instanceName":"1"});
            var Q42;
            Q42=makeQuery(id+"F3.opExtrude","SWEPT_EDGE",EDGE,{"disambiguationData":[OSD([sQuery(id+"F2.wireOp",EDGE,"E16"),sQuery(id+"F2.wireOp",EDGE,"E17")])]});
            fillet(context, id + "F14", {"entities" : qUnion([Q0, Q1, Q2, Q3, Q4, Q5, Q6, Q7, Q8, Q9, Q10, Q11, Q12, Q13, Q14, Q15, Q16, Q17, Q18, Q19, Q20, Q21, Q22, Q23, Q24, Q25, Q26, Q27, Q28, Q29, Q30, Q31, Q32, Q33, Q34, Q35, Q36, Q37, Q38, Q39, Q40, Q41, Q42]), "radius" : 1 * mm, "tangentPropagation" : true, "allowEdgeOverflow" : false});
        }
    });
